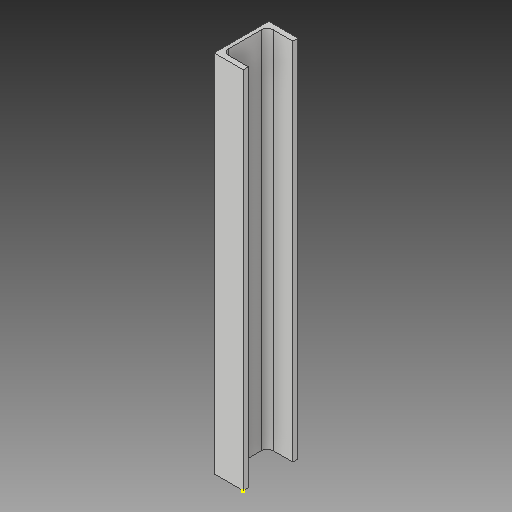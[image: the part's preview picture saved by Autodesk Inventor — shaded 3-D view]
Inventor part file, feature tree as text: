
AUTODESK INVENTOR PART (.ipt)
format: ipt  version: 2019 (Build 230136000, 136)  size: 93,184 bytes
history: native  units: in
note: dims shown in document units (in); Inventor stores cm internally (conversion verified against a paired STEP export)
features: other x3, sketch x2
ambient origin geometry x8: Origin, YZ Plane, XZ Plane, XY Plane, X Axis, Y Axis, Z Axis, Center Point
bodies: Solid1 (feature_tree)
feature tree (5):
  other  "Channel2_MIR.ipt"
  other  "Solid1::Channel2_MIR.ipt"
  other  "TaggingFeature1"
  sketch  "Sketch1"  dims[d0=0.3937in]
  sketch  "Sketch2"
